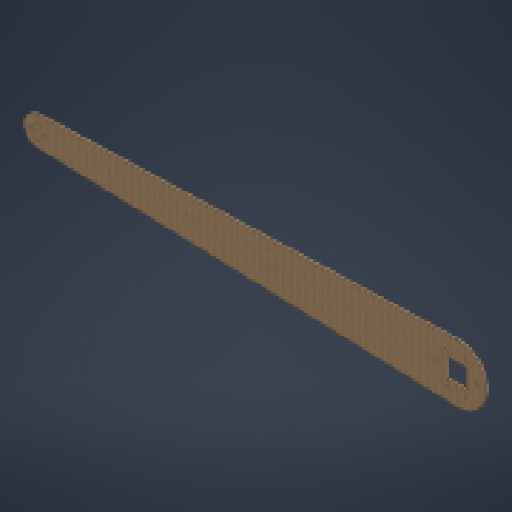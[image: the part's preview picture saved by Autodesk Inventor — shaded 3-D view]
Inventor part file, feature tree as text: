
AUTODESK INVENTOR PART (.ipt)
format: ipt  version: 2024.1 (Build 281209000, 209)  size: 173,056 bytes
history: native  units: in
note: dims shown in document units (in); Inventor stores cm internally (conversion verified against a paired STEP export)
features: other x2, extrude x1, sketch x1, reference x1
ambient origin geometry x8: Origin, YZ Plane, XZ Plane, XY Plane, X Axis, Y Axis, Z Axis, Center Point
bodies: Solid1 (feature_tree)
feature tree (5):
  extrude  "Extrusion1"  Depth=21.6535in
  sketch  "Sketch1"  dims[d0=3.0in d1=21.6535in d2=1.5in d3=0.1575in d4=0.375in d5=1.5748in d7=360.0deg d9=0.1575in d10=0.1575in d11=0.1575in d12=0.1575in d13=0.1575in d14=0.1575in d15=0.125in d16=0.0in]
  reference  "Reference1"
  other  "Assembly1"
  other  "ArmPivot:1"
